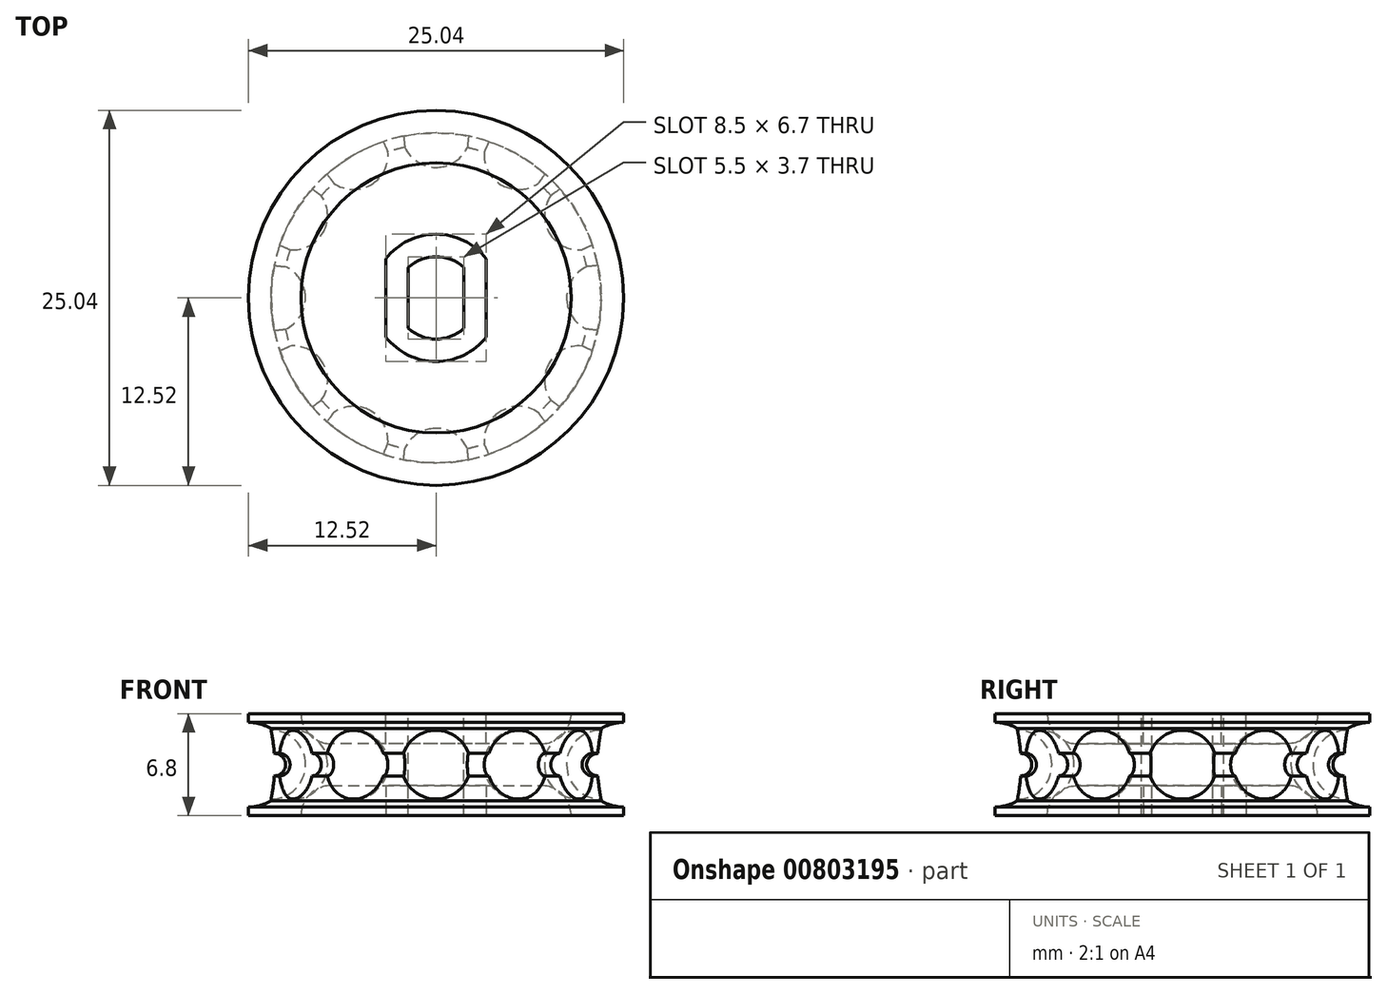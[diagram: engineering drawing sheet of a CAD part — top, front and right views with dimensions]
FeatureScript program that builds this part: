
annotation { "Feature Type Name" : "Feature", "Feature Type Description" : "" }
export const myFeature = defineFeature(function(context is Context, id is Id, definition is map)
    precondition{}
    {
        {
            var Q0;
            Q0=qCreatedBy(makeId("Top.planeOp"),FACE);
            var sketch = newSketch(context, id + "F0", { "sketchPlane" : qUnion([Q0])});
            skCircle(sketch, "E0", {"center": v(0, 0) * mm, "radius": 11.02 * mm});
            skSolve(sketch);
        }
        {
            var Q0;
            Q0=qCreatedBy(makeId("Top.planeOp"),FACE);
            var sketch = newSketch(context, id + "F1", { "sketchPlane" : qUnion([Q0])});
            skArc(sketch, "E1", {"start": v(0, 13.32) * mm, "mid": v(-2.3, 11.02) * mm, "end": v(0, 8.72) * mm});
            skLineSegment(sketch, "E2", {"start": v(0, 13.32) * mm, "end": v(0, 8.72) * mm});
            skSolve(sketch);
        }
        {
            var Q0;
            Q0=makeQuery(id+"F1.imprint","IMPRINT",FACE,{"disambiguationData":[TD([[makeQuery(id+"F1.imprint","IMPRINT",EDGE,{"derivedFrom":sQuery(id+"F1.wireOp",EDGE,"E1")}),1.0]])]});
            var Q1;
            Q1=sQuery(id+"F1.wireOp",EDGE,"E1");
            var Q2;
            Q2=sQuery(id+"F1.wireOp",EDGE,"E2");
            revolve(context, id + "F2", {"surfaceOperationType" : NewSurfaceOperationType.NEW, "entities" : qUnion([Q0]), "surfaceEntities" : qUnion([Q1]), "axis" : qUnion([Q2]), "revolveType" : RevolveType.FULL});
        }
        {
            var Q0;
            Q0=makeQuery(id+"F2.opRevolve","SWEPT_BODY",BODY,{"disambiguationData":[OSD([sQuery(id+"F1.wireOp",EDGE,"E1")])]});
            var Q1;
            Q1=sQuery(id+"F0.wireOp",EDGE,"E0");
            circularPattern(context, id + "F3", {"entities" : qUnion([Q0]), "axis" : qUnion([Q1]), "angle" : 360 * degree, "instanceCount" : 12, "equalSpace" : true});
        }
        {
            var Q0;
            Q0 = qSketchRegion(id + "F0", true);
            extrude(context, id + "F4", {"entities" : qUnion([Q0]), "depth" : 2.4 * mm, "offsetDistance" : 25 * mm, "hasSecondDirection" : true, "secondDirectionOppositeDirection" : true, "secondDirectionDepth" : 2.4 * mm});
        }
        {
            var Q0;
            Q0=makeQuery(id+"F3.opPattern","COPY",BODY,{"derivedFrom":makeQuery(id+"F2.opRevolve","SWEPT_BODY",BODY,{"disambiguationData":[OSD([sQuery(id+"F1.wireOp",EDGE,"E1"),sQuery(id+"F1.wireOp",EDGE,"E2")])]}),"instanceName":"11"});
            var Q1;
            Q1=makeQuery(id+"F3.opPattern","COPY",BODY,{"derivedFrom":makeQuery(id+"F2.opRevolve","SWEPT_BODY",BODY,{"disambiguationData":[OSD([sQuery(id+"F1.wireOp",EDGE,"E1"),sQuery(id+"F1.wireOp",EDGE,"E2")])]}),"instanceName":"10"});
            var Q2;
            Q2=makeQuery(id+"F3.opPattern","COPY",BODY,{"derivedFrom":makeQuery(id+"F2.opRevolve","SWEPT_BODY",BODY,{"disambiguationData":[OSD([sQuery(id+"F1.wireOp",EDGE,"E1"),sQuery(id+"F1.wireOp",EDGE,"E2")])]}),"instanceName":"9"});
            var Q3;
            Q3=makeQuery(id+"F3.opPattern","COPY",BODY,{"derivedFrom":makeQuery(id+"F2.opRevolve","SWEPT_BODY",BODY,{"disambiguationData":[OSD([sQuery(id+"F1.wireOp",EDGE,"E1"),sQuery(id+"F1.wireOp",EDGE,"E2")])]}),"instanceName":"8"});
            var Q4;
            Q4=makeQuery(id+"F2.opRevolve","SWEPT_BODY",BODY,{"disambiguationData":[OSD([sQuery(id+"F1.wireOp",EDGE,"E1"),sQuery(id+"F1.wireOp",EDGE,"E2")])]});
            var Q5;
            Q5=makeQuery(id+"F3.opPattern","COPY",BODY,{"derivedFrom":makeQuery(id+"F2.opRevolve","SWEPT_BODY",BODY,{"disambiguationData":[OSD([sQuery(id+"F1.wireOp",EDGE,"E1"),sQuery(id+"F1.wireOp",EDGE,"E2")])]}),"instanceName":"1"});
            var Q6;
            Q6=makeQuery(id+"F3.opPattern","COPY",BODY,{"derivedFrom":makeQuery(id+"F2.opRevolve","SWEPT_BODY",BODY,{"disambiguationData":[OSD([sQuery(id+"F1.wireOp",EDGE,"E1"),sQuery(id+"F1.wireOp",EDGE,"E2")])]}),"instanceName":"2"});
            var Q7;
            Q7=makeQuery(id+"F3.opPattern","COPY",BODY,{"derivedFrom":makeQuery(id+"F2.opRevolve","SWEPT_BODY",BODY,{"disambiguationData":[OSD([sQuery(id+"F1.wireOp",EDGE,"E1"),sQuery(id+"F1.wireOp",EDGE,"E2")])]}),"instanceName":"3"});
            var Q8;
            Q8=makeQuery(id+"F3.opPattern","COPY",BODY,{"derivedFrom":makeQuery(id+"F2.opRevolve","SWEPT_BODY",BODY,{"disambiguationData":[OSD([sQuery(id+"F1.wireOp",EDGE,"E1"),sQuery(id+"F1.wireOp",EDGE,"E2")])]}),"instanceName":"4"});
            var Q9;
            Q9=makeQuery(id+"F3.opPattern","COPY",BODY,{"derivedFrom":makeQuery(id+"F2.opRevolve","SWEPT_BODY",BODY,{"disambiguationData":[OSD([sQuery(id+"F1.wireOp",EDGE,"E1"),sQuery(id+"F1.wireOp",EDGE,"E2")])]}),"instanceName":"5"});
            var Q10;
            Q10=makeQuery(id+"F3.opPattern","COPY",BODY,{"derivedFrom":makeQuery(id+"F2.opRevolve","SWEPT_BODY",BODY,{"disambiguationData":[OSD([sQuery(id+"F1.wireOp",EDGE,"E1"),sQuery(id+"F1.wireOp",EDGE,"E2")])]}),"instanceName":"6"});
            var Q11;
            Q11=makeQuery(id+"F3.opPattern","COPY",BODY,{"derivedFrom":makeQuery(id+"F2.opRevolve","SWEPT_BODY",BODY,{"disambiguationData":[OSD([sQuery(id+"F1.wireOp",EDGE,"E1"),sQuery(id+"F1.wireOp",EDGE,"E2")])]}),"instanceName":"7"});
            var Q12;
            Q12=makeQuery(id+"F4.opExtrude","SWEPT_BODY",BODY,{"disambiguationData":[OSD([sQuery(id+"F0.wireOp",EDGE,"E0")])]});
            booleanBodies(context, id + "F5", {"operationType" : BooleanOperationType.SUBTRACTION, "tools" : qUnion([Q0, Q1, Q2, Q3, Q4, Q5, Q6, Q7, Q8, Q9, Q10, Q11]), "targets" : qUnion([Q12])});
        }
        {
            var Q0;
            Q0=qCreatedBy(makeId("Right.planeOp"),FACE);
            var sketch = newSketch(context, id + "F6", { "sketchPlane" : qUnion([Q0])});
            skCircle(sketch, "E3", {"center": v(-11.02, 0) * mm, "radius": 0.75 * mm});
            skLineSegment(sketch, "E4.0", {"start": v(-11.02, 0) * mm, "end": v(11.02, 0) * mm});
            skSolve(sketch);
        }
        {
            var Q0;
            Q0 = qSketchRegion(id + "F6", true);
            var Q1;
            Q1=sQuery(id+"F0.wireOp",EDGE,"E0");
            revolve(context, id + "F7", {"surfaceOperationType" : NewSurfaceOperationType.NEW, "entities" : qUnion([Q0]), "axis" : qUnion([Q1]), "revolveType" : RevolveType.FULL});
        }
        {
            var Q0;
            Q0=makeQuery(id+"F7.opRevolve","SWEPT_BODY",BODY,{"disambiguationData":[OSD([sQuery(id+"F6.wireOp",EDGE,"E3")])]});
            var Q1;
            Q1=makeQuery(id+"F4.opExtrude","SWEPT_BODY",BODY,{"disambiguationData":[OSD([sQuery(id+"F0.wireOp",EDGE,"E0")])]});
            booleanBodies(context, id + "F8", {"operationType" : BooleanOperationType.SUBTRACTION, "tools" : qUnion([Q0]), "targets" : qUnion([Q1])});
        }
        {
            var Q0;
            Q0=qCreatedBy(makeId("Right.planeOp"),FACE);
            var sketch = newSketch(context, id + "F9", { "sketchPlane" : qUnion([Q0])});
            skLineSegment(sketch, "E5.0", {"start": v(-11.02, 2.4) * mm, "end": v(11.02, 2.4) * mm});
            skLineSegment(sketch, "E6", {"start": v(0, 2.4) * mm, "end": v(0, 3.4) * mm});
            skLineSegment(sketch, "E7", {"start": v(0, 3.4) * mm, "end": v(12.52, 3.4) * mm});
            skLineSegment(sketch, "E8", {"start": v(12.52, 3.4) * mm, "end": v(12.52, 2.83) * mm});
            skArc(sketch, "E9", {"start": v(12.52, 2.83) * mm, "mid": v(11.74, 2.72) * mm, "end": v(11.02, 2.4) * mm});
            skArc(sketch, "E10.MirrorCS", {"start": v(12.52, -2.83) * mm, "mid": v(11.74, -2.72) * mm, "end": v(11.02, -2.4) * mm});
            skLineSegment(sketch, "E11.MirrorCS", {"start": v(12.52, -3.4) * mm, "end": v(12.52, -2.83) * mm});
            skLineSegment(sketch, "E12.MirrorCS", {"start": v(-11.02, -2.4) * mm, "end": v(11.02, -2.4) * mm});
            skLineSegment(sketch, "E13.MirrorCS", {"start": v(0, -3.4) * mm, "end": v(12.52, -3.4) * mm});
            skLineSegment(sketch, "E14.MirrorCS", {"start": v(0, -2.4) * mm, "end": v(0, -3.4) * mm});
            skSolve(sketch);
        }
        {
            var Q0;
            Q0 = qSketchRegion(id + "F9", true);
            var Q1;
            Q1=sQuery(id+"F9.wireOp",EDGE,"E6");
            revolve(context, id + "F10", {"operationType" : NewBodyOperationType.ADD, "surfaceOperationType" : NewSurfaceOperationType.NEW, "entities" : qUnion([Q0]), "axis" : qUnion([Q1]), "revolveType" : RevolveType.FULL});
        }
        {
            var Q0;
            Q0=makeQuery(id+"F10.opRevolve","SWEPT_FACE",FACE,{"disambiguationData":[OSD([sQuery(id+"F9.wireOp",EDGE,"E7")])]});
            var sketch = newSketch(context, id + "F11", { "sketchPlane" : qUnion([Q0])});
            skArc(sketch, "E15", {"start": v(1.85, 2.03) * mm, "mid": v(0, 2.75) * mm, "end": v(-1.85, 2.03) * mm});
            skLineSegment(sketch, "E16.left", {"start": v(-1.85, 2.03) * mm, "end": v(-1.85, -2.03) * mm});
            skLineSegment(sketch, "E16.right", {"start": v(1.85, 2.03) * mm, "end": v(1.85, -2.03) * mm});
            skArc(sketch, "E17.trimOffspring", {"start": v(-1.85, -2.03) * mm, "mid": v(0, -2.75) * mm, "end": v(1.85, -2.03) * mm});
            skSolve(sketch);
        }
        {
            var Q0;
            Q0 = qSketchRegion(id + "F11", true);
            extrude(context, id + "F12", {"entities" : qUnion([Q0]), "operationType" : NewBodyOperationType.REMOVE, "endBound" : BoundingType.THROUGH_ALL, "oppositeDirection" : true, "depth" : 25 * mm, "offsetDistance" : 25 * mm});
        }
        {
            var Q0;
            Q0=makeQuery(id+"F10.opRevolve","SWEPT_FACE",FACE,{"disambiguationData":[OSD([sQuery(id+"F9.wireOp",EDGE,"E13.MirrorCS")])]});
            var sketch = newSketch(context, id + "F13", { "sketchPlane" : qUnion([Q0])});
            skCircle(sketch, "E18.0", {"center": v(0, 0) * mm, "radius": 9.02 * mm});
            skArc(sketch, "E19.0", {"start": v(3.35, 2.62) * mm, "mid": v(0, 4.25) * mm, "end": v(-3.35, 2.62) * mm});
            skLineSegment(sketch, "E19.1", {"start": v(3.35, 2.62) * mm, "end": v(3.35, -2.62) * mm});
            skArc(sketch, "E19.2", {"start": v(-3.35, -2.62) * mm, "mid": v(0, -4.25) * mm, "end": v(3.35, -2.62) * mm});
            skLineSegment(sketch, "E19.3", {"start": v(-3.35, 2.62) * mm, "end": v(-3.35, -2.62) * mm});
            skSolve(sketch);
        }
        {
            var Q0;
            Q0 = qSketchRegion(id + "F13", true);
            extrude(context, id + "F14", {"entities" : qUnion([Q0]), "oppositeDirection" : true, "depth" : 2 * mm, "offsetDistance" : 25 * mm});
        }
        {
            var Q0;
            Q0=makeQuery(id+"F14.opExtrude","SWEPT_BODY",BODY,{"disambiguationData":[OSD([sQuery(id+"F13.wireOp",EDGE,"E18.0"),sQuery(id+"F13.wireOp",EDGE,"E19.0"),sQuery(id+"F13.wireOp",EDGE,"E19.1"),sQuery(id+"F13.wireOp",EDGE,"E19.2"),sQuery(id+"F13.wireOp",EDGE,"E19.3")])]});
            var Q1;
            Q1=qCreatedBy(makeId("Top.planeOp"),FACE);
            mirror(context, id + "F15", {"entities" : qUnion([Q0]), "mirrorPlane" : qUnion([Q1])});
        }
        {
            var Q0;
            Q0=makeQuery(id+"F14.opExtrude","SWEPT_BODY",BODY,{"disambiguationData":[OSD([sQuery(id+"F13.wireOp",EDGE,"E18.0"),sQuery(id+"F13.wireOp",EDGE,"E19.0"),sQuery(id+"F13.wireOp",EDGE,"E19.1"),sQuery(id+"F13.wireOp",EDGE,"E19.2"),sQuery(id+"F13.wireOp",EDGE,"E19.3")])]});
            var Q1;
            Q1=makeQuery(id+"F15.opPattern","COPY",BODY,{"derivedFrom":makeQuery(id+"F14.opExtrude","SWEPT_BODY",BODY,{"disambiguationData":[OSD([sQuery(id+"F13.wireOp",EDGE,"E18.0"),sQuery(id+"F13.wireOp",EDGE,"E19.0"),sQuery(id+"F13.wireOp",EDGE,"E19.1"),sQuery(id+"F13.wireOp",EDGE,"E19.2"),sQuery(id+"F13.wireOp",EDGE,"E19.3")])]}),"instanceName":"1"});
            var Q2;
            Q2=makeQuery(id+"F4.opExtrude","SWEPT_BODY",BODY,{"disambiguationData":[OSD([sQuery(id+"F0.wireOp",EDGE,"E0")])]});
            booleanBodies(context, id + "F16", {"operationType" : BooleanOperationType.SUBTRACTION, "tools" : qUnion([Q0, Q1]), "targets" : qUnion([Q2])});
        }
        {
            var Q0;
            Q0=makeQuery(id+"F16.opBoolean","COPY",EDGE,{"derivedFrom":makeQuery(id+"F14.opExtrude","CAP_EDGE",EDGE,{"disambiguationData":[OSD([sQuery(id+"F13.wireOp",EDGE,"E18.0")])],"isStart":false})});
            fillet(context, id + "F17", {"entities" : qUnion([Q0]), "radius" : 2 * mm, "tangentPropagation" : true, "allowEdgeOverflow" : false});
        }
        {
            var Q0;
            Q0=makeQuery(id+"F16.opBoolean","COPY",EDGE,{"derivedFrom":makeQuery(id+"F15.opPattern","COPY",EDGE,{"derivedFrom":makeQuery(id+"F14.opExtrude","CAP_EDGE",EDGE,{"disambiguationData":[OSD([sQuery(id+"F13.wireOp",EDGE,"E18.0")])],"isStart":false}),"instanceName":"1"})});
            fillet(context, id + "F18", {"entities" : qUnion([Q0]), "radius" : 2 * mm, "tangentPropagation" : true, "allowEdgeOverflow" : false});
        }
    });
